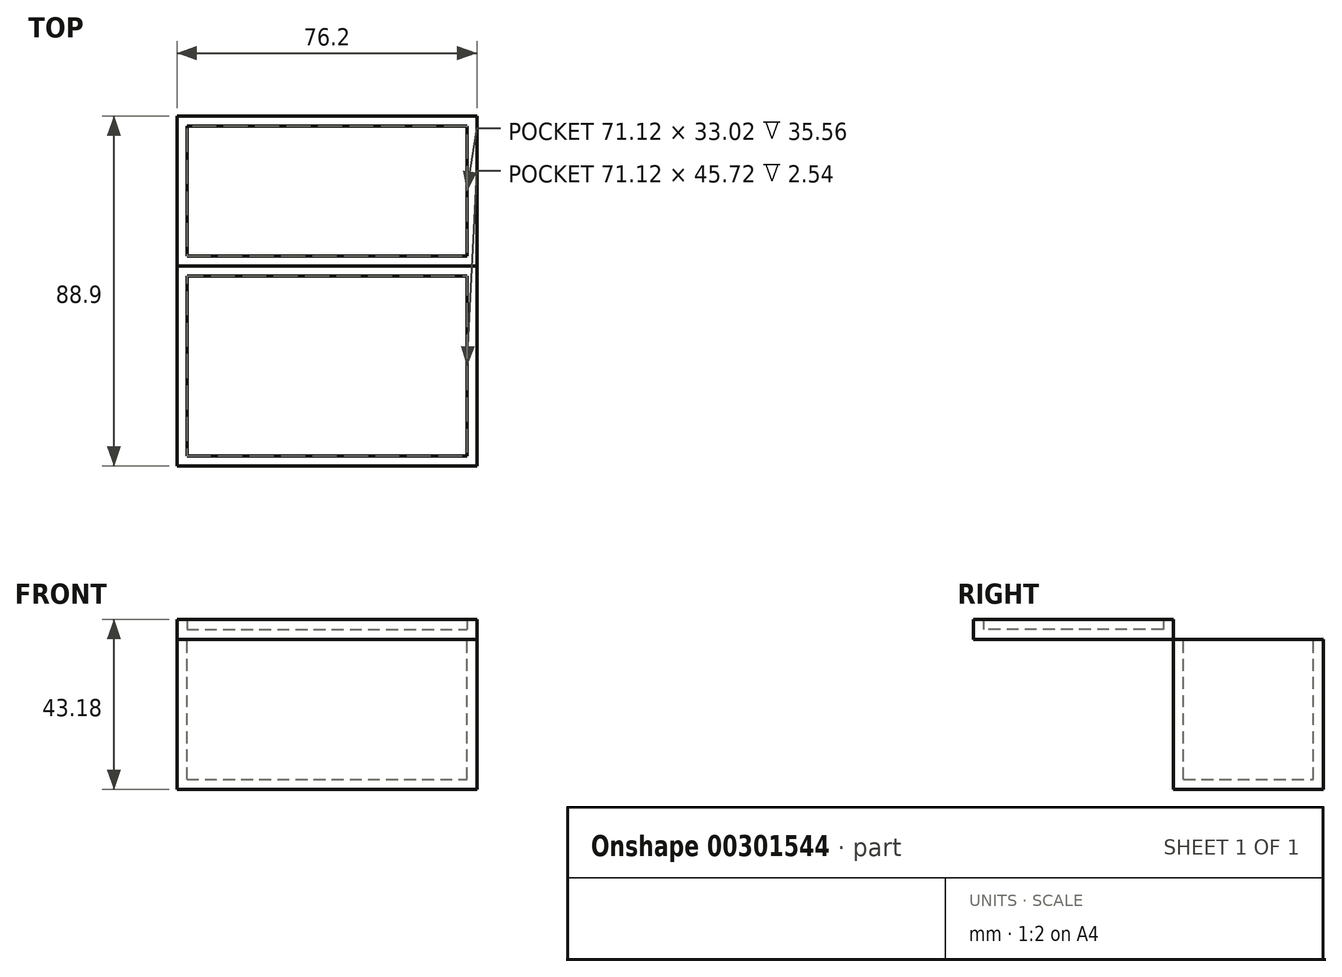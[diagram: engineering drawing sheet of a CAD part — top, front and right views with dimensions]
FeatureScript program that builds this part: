
annotation { "Feature Type Name" : "Feature", "Feature Type Description" : "" }
export const myFeature = defineFeature(function(context is Context, id is Id, definition is map)
    precondition{}
    {
        {
            var Q0;
            Q0=qCreatedBy(makeId("Top.planeOp"),FACE);
            var sketch = newSketch(context, id + "F0", { "sketchPlane" : qUnion([Q0])});
            skLineSegment(sketch, "E0", {"start": v(0, 0) * mm, "end": v(-38.1, 0) * mm, "construction": true});
            skLineSegment(sketch, "E1", {"start": v(0, 0) * mm, "end": v(38.1, 0) * mm, "construction": true});
            skLineSegment(sketch, "E2", {"start": v(0, 0) * mm, "end": v(0, -50.8) * mm, "construction": true});
            skLineSegment(sketch, "E3", {"start": v(-38.1, 0) * mm, "end": v(-38.1, 38.1) * mm});
            skLineSegment(sketch, "E4", {"start": v(38.1, 0) * mm, "end": v(38.1, 38.1) * mm});
            skLineSegment(sketch, "E5", {"start": v(-38.1, 0) * mm, "end": v(-38.1, -50.8) * mm});
            skLineSegment(sketch, "E6", {"start": v(38.1, 0) * mm, "end": v(38.1, -50.8) * mm});
            skLineSegment(sketch, "E7", {"start": v(-38.1, 38.1) * mm, "end": v(38.1, 38.1) * mm});
            skLineSegment(sketch, "E8", {"start": v(-38.1, -50.8) * mm, "end": v(38.1, -50.8) * mm});
            skLineSegment(sketch, "E9", {"start": v(-38.1, 0) * mm, "end": v(38.1, 0) * mm});
            skSolve(sketch);
        }
        {
            var Q0;
            Q0=makeQuery(id+"F0.imprint","IMPRINT",FACE,{"disambiguationData":[TD([[makeQuery(id+"F0.imprint","IMPRINT",EDGE,{"derivedFrom":sQuery(id+"F0.wireOp",EDGE,"E5")}),1.0]])]});
            extrude(context, id + "F1", {"entities" : qUnion([Q0]), "depth" : 5.08 * mm});
        }
        {
            var Q0;
            Q0=makeQuery(id+"F0.imprint","IMPRINT",FACE,{"disambiguationData":[TD([[makeQuery(id+"F0.imprint","IMPRINT",EDGE,{"derivedFrom":sQuery(id+"F0.wireOp",EDGE,"E3")}),-1.0]])]});
            extrude(context, id + "F2", {"entities" : qUnion([Q0]), "oppositeDirection" : true, "depth" : 38.1 * mm});
        }
        {
            var Q0;
            Q0=makeQuery(id+"F2.opExtrude","CAP_FACE",FACE,{"disambiguationData":[OSD([sQuery(id+"F0.wireOp",EDGE,"E3"),sQuery(id+"F0.wireOp",EDGE,"E4"),sQuery(id+"F0.wireOp",EDGE,"E7"),sQuery(id+"F0.wireOp",EDGE,"E9")])],"isStart":true});
            var Q1;
            Q1=makeQuery(id+"F1.opExtrude","CAP_FACE",FACE,{"disambiguationData":[OSD([sQuery(id+"F0.wireOp",EDGE,"E5"),sQuery(id+"F0.wireOp",EDGE,"E6"),sQuery(id+"F0.wireOp",EDGE,"E8"),sQuery(id+"F0.wireOp",EDGE,"E9")])],"isStart":false});
            shell(context, id + "F3", {"entities" : qUnion([Q0, Q1]), "thickness" : 2.54 * mm});
        }
    });
